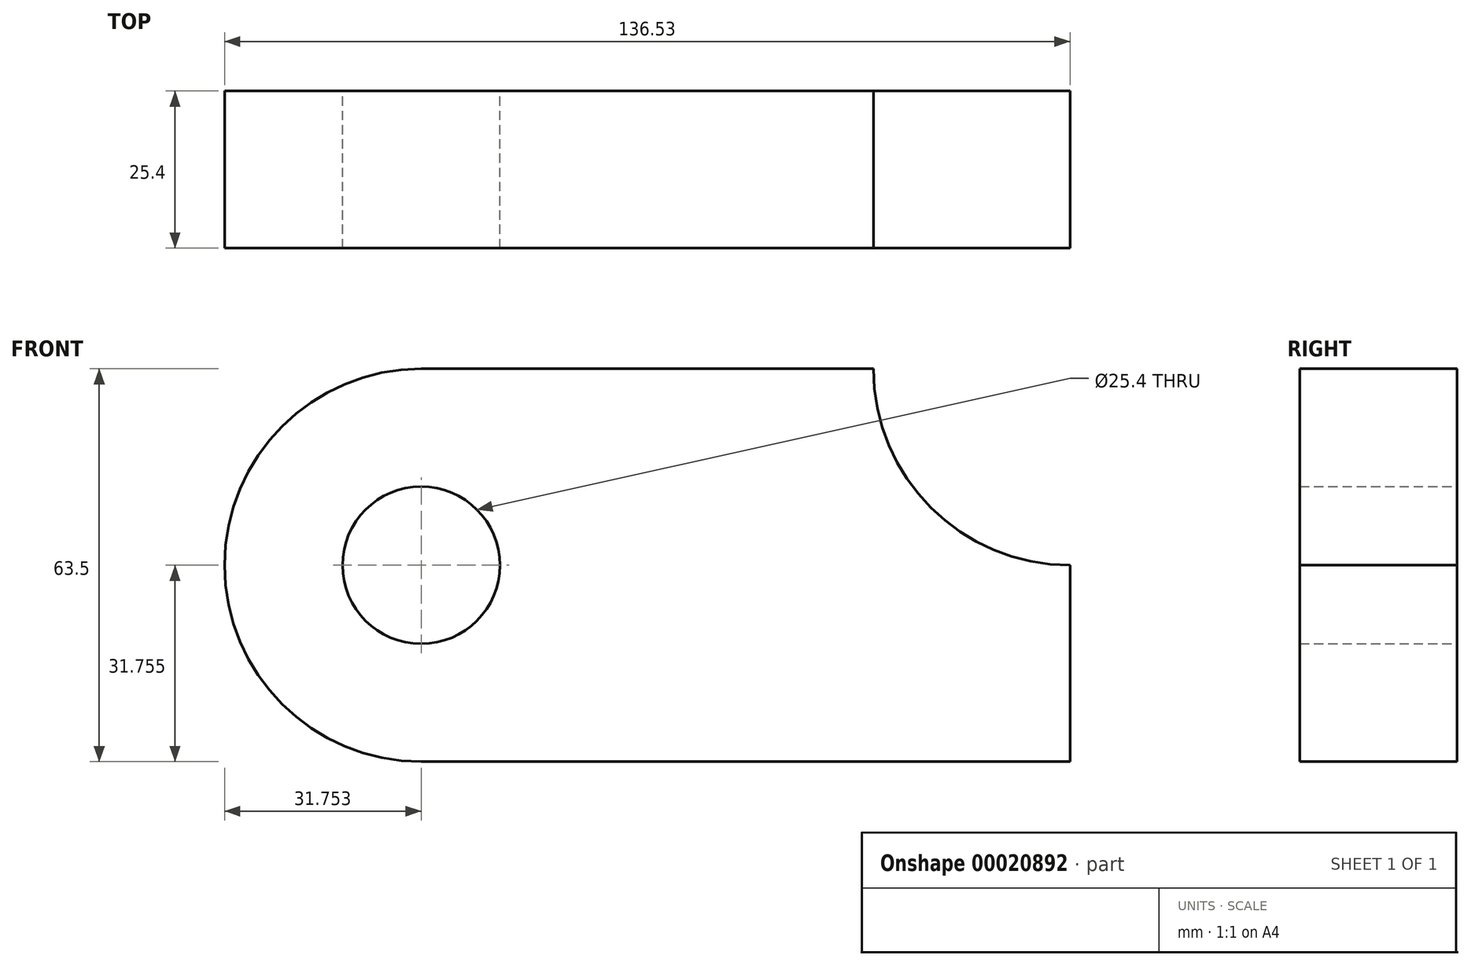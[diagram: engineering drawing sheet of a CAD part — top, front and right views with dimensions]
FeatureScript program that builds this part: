
annotation { "Feature Type Name" : "Feature", "Feature Type Description" : "" }
export const myFeature = defineFeature(function(context is Context, id is Id, definition is map)
    precondition{}
    {
        {
            var Q0;
            Q0=qCreatedBy(makeId("Front.planeOp"),FACE);
            var sketch = newSketch(context, id + "F0", { "sketchPlane" : qUnion([Q0])});
            skLineSegment(sketch, "E0.bottom", {"start": v(-89.4, 22.2) * mm, "end": v(15.38, 22.2) * mm});
            skLineSegment(sketch, "E0.top", {"start": v(-89.4, -41.3) * mm, "end": v(15.38, -41.3) * mm});
            skLineSegment(sketch, "E0.left", {"start": v(-89.4, 22.2) * mm, "end": v(-89.4, -41.3) * mm});
            skLineSegment(sketch, "E0.right", {"start": v(15.38, 22.2) * mm, "end": v(15.38, -41.3) * mm});
            skCircle(sketch, "E1", {"center": v(-89.4, -9.56) * mm, "radius": 31.75 * mm});
            skCircle(sketch, "E2", {"center": v(-89.4, -9.56) * mm, "radius": 12.7 * mm});
            skArc(sketch, "E3", {"start": v(-16.37, 22.2) * mm, "mid": v(-7.07, -0.26) * mm, "end": v(15.38, -9.56) * mm});
            skSolve(sketch);
        }
        {
            var Q0;
            {var subQ0=sQuery(id+"F0.wireOp",EDGE,"E2");var subQ1=sQuery(id+"F0.wireOp",EDGE,"E0.left");var subQ3=makeQuery(id+"F0.imprint","INTERSECT",VERTEX,{"disambiguationData":[OD(0.0)],"derivedFrom":[subQ1,subQ0]});Q0=makeQuery(id+"F0.imprint","IMPRINT",FACE,{"disambiguationData":[TD([[makeQuery(id+"F0.imprint","IMPRINT",EDGE,{"disambiguationData":[TD([[subQ3,-1.0]])],"derivedFrom":subQ0}),-1.0]])]});}
            var Q1;
            {var subQ0=sQuery(id+"F0.wireOp",EDGE,"E2");var subQ1=sQuery(id+"F0.wireOp",EDGE,"E0.left");var subQ3=makeQuery(id+"F0.imprint","INTERSECT",VERTEX,{"disambiguationData":[OD(0.0)],"derivedFrom":[subQ1,subQ0]});Q1=makeQuery(id+"F0.imprint","IMPRINT",FACE,{"disambiguationData":[TD([[makeQuery(id+"F0.imprint","IMPRINT",EDGE,{"disambiguationData":[TD([[subQ3,1.0]])],"derivedFrom":subQ0}),-1.0]])]});}
            var Q2;
            {var subQ6=sQuery(id+"F0.wireOp",EDGE,"E0.top");Q2=makeQuery(id+"F0.imprint","IMPRINT",FACE,{"disambiguationData":[TD([[makeQuery(id+"F0.imprint","IMPRINT",EDGE,{"derivedFrom":subQ6}),1.0]])]});}
            extrude(context, id + "F1", {"entities" : qUnion([Q0, Q1, Q2]), "depth" : 25.4 * mm});
        }
    });
